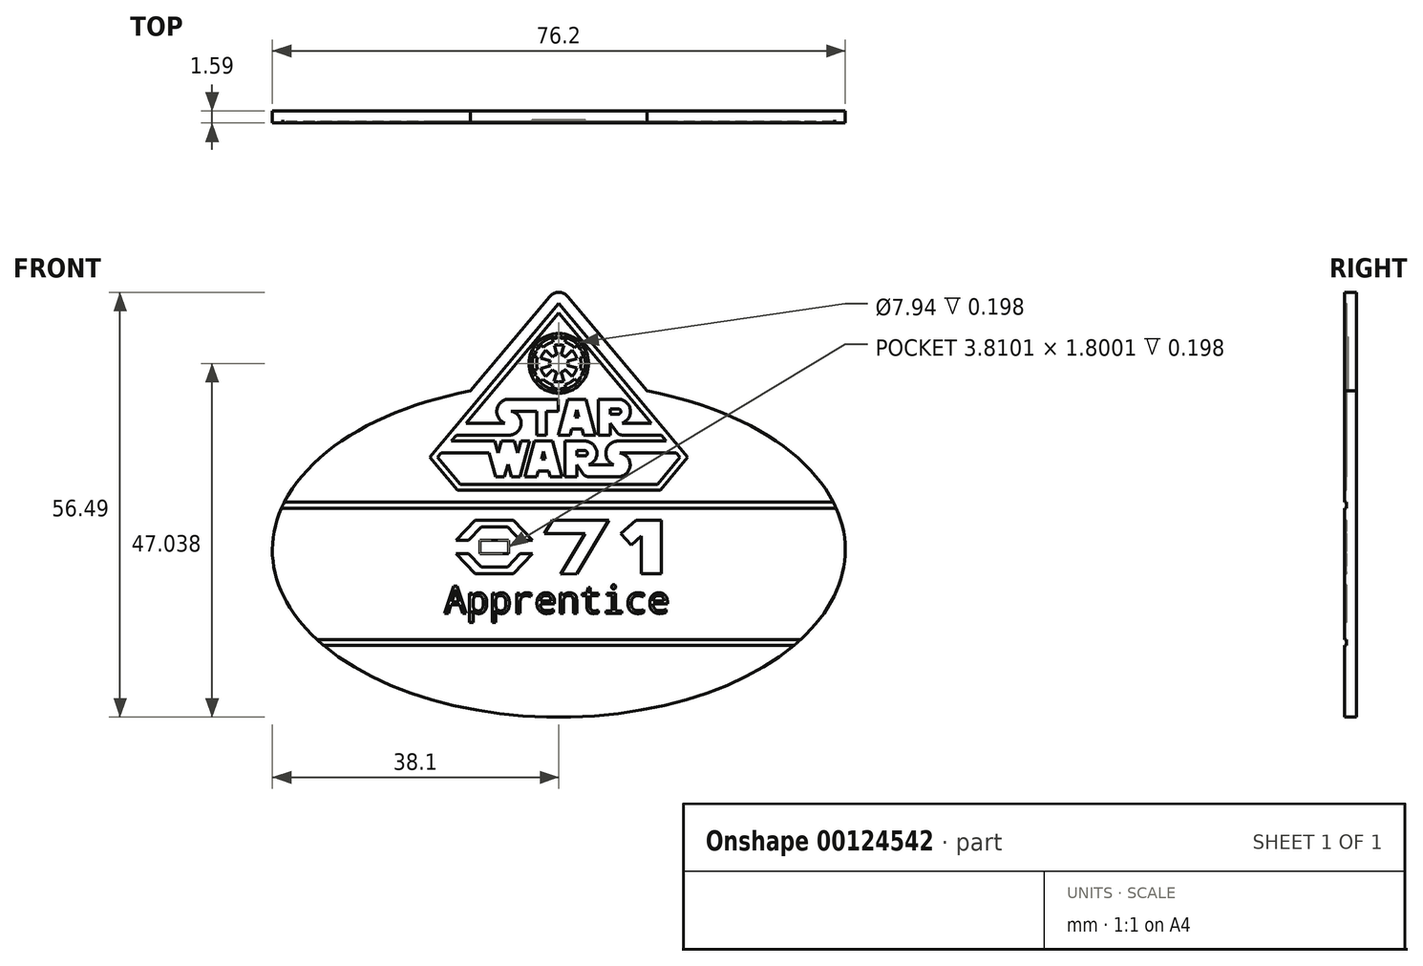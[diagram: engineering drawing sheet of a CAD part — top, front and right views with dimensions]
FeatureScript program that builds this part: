
annotation { "Feature Type Name" : "Feature", "Feature Type Description" : "" }
export const myFeature = defineFeature(function(context is Context, id is Id, definition is map)
    precondition{}
    {
        {
            var Q0;
            Q0=qCreatedBy(makeId("Front.planeOp"),FACE);
            var sketch = newSketch(context, id + "F0", { "sketchPlane" : qUnion([Q0])});
            skLineSegment(sketch, "E0", {"start": v(36.9, 5.56) * mm, "end": v(-36.9, 5.56) * mm});
            skLineSegment(sketch, "E1", {"start": v(-36.51, 6.35) * mm, "end": v(36.51, 6.35) * mm});
            skPoint(sketch, "E2", {"position": v(0, 35.14) * mm});
            skLineSegment(sketch, "E3.trimOffspring", {"start": v(0, 22.22) * mm, "end": v(0, 22.22) * mm});
            skPoint(sketch, "E4", {"position": v(0, -22.23) * mm});
            skPoint(sketch, "E5", {"position": v(-13.5, 7.94) * mm});
            skPoint(sketch, "E6", {"position": v(13.5, 7.94) * mm});
            skLineSegment(sketch, "E7", {"start": v(0, 35.14) * mm, "end": v(11.75, 21.14) * mm});
            skLineSegment(sketch, "E8", {"start": v(0, 35.14) * mm, "end": v(-11.75, 21.14) * mm});
            skEllipticalArc(sketch, "E9", {});
            skLineSegment(sketch, "E10", {"start": v(0, 32.76) * mm, "end": v(-17.16, 12.3) * mm});
            skLineSegment(sketch, "E11", {"start": v(0, 32.76) * mm, "end": v(17.16, 12.3) * mm});
            skPoint(sketch, "E12", {"position": v(0, 7.97) * mm});
            skLineSegment(sketch, "E13", {"start": v(-13.5, 7.94) * mm, "end": v(-17.16, 12.3) * mm});
            skLineSegment(sketch, "E14", {"start": v(13.5, 7.94) * mm, "end": v(17.16, 12.3) * mm});
            skLineSegment(sketch, "E15", {"start": v(-13.5, 7.94) * mm, "end": v(13.5, 7.94) * mm});
            skLineSegment(sketch, "E16.trimOffspring", {"start": v(0, 7.97) * mm, "end": v(0, 7.94) * mm});
            skLineSegment(sketch, "E17.trimOffspring", {"start": v(0, 0) * mm, "end": v(0, 0) * mm});
            skLineSegment(sketch, "E18.trimOffspring", {"start": v(0, -22.23) * mm, "end": v(0, -22.23) * mm});
            skLineSegment(sketch, "E19.0", {"start": v(-13.12, 8.73) * mm, "end": v(-16.13, 12.3) * mm});
            skLineSegment(sketch, "E19.1", {"start": v(0, 31.53) * mm, "end": v(-16.13, 12.3) * mm});
            skLineSegment(sketch, "E19.2", {"start": v(-13.12, 8.73) * mm, "end": v(13.12, 8.73) * mm});
            skLineSegment(sketch, "E19.3", {"start": v(13.12, 8.73) * mm, "end": v(16.13, 12.3) * mm});
            skLineSegment(sketch, "E19.4", {"start": v(0, 31.53) * mm, "end": v(16.13, 12.3) * mm});
            skCircle(sketch, "E20", {"center": v(0, 24.8) * mm, "radius": 3.97 * mm});
            skLineSegment(sketch, "E21", {"start": v(0, 18.51) * mm, "end": v(0, 7.97) * mm});
            skLineSegment(sketch, "E22", {"start": v(-31.27, -12.7) * mm, "end": v(31.27, -12.7) * mm});
            skLineSegment(sketch, "E23", {"start": v(-32.17, -11.9) * mm, "end": v(32.17, -11.9) * mm});
            skArc(sketch, "E24", {"start": v(2.98, 26.72) * mm, "mid": v(1.77, 27.87) * mm, "end": v(0.17, 28.34) * mm});
            skArc(sketch, "E25", {"start": v(-0.17, 28.19) * mm, "mid": v(-0.52, 28.15) * mm, "end": v(-0.86, 28.08) * mm});
            skArc(sketch, "E26", {"start": v(-1.73, 26.57) * mm, "mid": v(-2.13, 26.06) * mm, "end": v(-2.38, 25.46) * mm});
            skArc(sketch, "E27", {"start": v(-0.74, 27.67) * mm, "mid": v(-1.45, 27.38) * mm, "end": v(-2.06, 26.92) * mm});
            skLineSegment(sketch, "E28", {"start": v(-0.17, 28.34) * mm, "end": v(-0.17, 28.19) * mm});
            skLineSegment(sketch, "E29", {"start": v(0.17, 28.34) * mm, "end": v(0.17, 28.19) * mm});
            skLineSegment(sketch, "E30", {"start": v(2.98, 26.72) * mm, "end": v(2.85, 26.64) * mm});
            skLineSegment(sketch, "E31", {"start": v(3.15, 26.42) * mm, "end": v(3.01, 26.35) * mm});
            skLineSegment(sketch, "E32", {"start": v(3.02, 23.28) * mm, "end": v(3.16, 23.21) * mm});
            skLineSegment(sketch, "E33", {"start": v(2.86, 23) * mm, "end": v(2.99, 22.91) * mm});
            skLineSegment(sketch, "E34", {"start": v(-0.86, 28.08) * mm, "end": v(-0.74, 27.67) * mm});
            skLineSegment(sketch, "E35", {"start": v(0.91, 28.07) * mm, "end": v(0.8, 27.65) * mm});
            skLineSegment(sketch, "E36.trimOffspring", {"start": v(0.67, 27.19) * mm, "end": v(0.33, 25.96) * mm});
            skLineSegment(sketch, "E37.trimOffspring", {"start": v(-0.61, 27.2) * mm, "end": v(-0.28, 25.98) * mm});
            skLineSegment(sketch, "E38", {"start": v(-0.87, 21.54) * mm, "end": v(-0.76, 21.95) * mm});
            skLineSegment(sketch, "E39", {"start": v(0.32, 23.65) * mm, "end": v(0.66, 22.43) * mm});
            skLineSegment(sketch, "E40", {"start": v(0.87, 23.98) * mm, "end": v(1.76, 23.07) * mm});
            skLineSegment(sketch, "E41", {"start": v(1.16, 24.5) * mm, "end": v(2.39, 24.18) * mm});
            skLineSegment(sketch, "E42", {"start": v(1.16, 25.13) * mm, "end": v(2.39, 25.45) * mm});
            skLineSegment(sketch, "E43", {"start": v(2.4, 27.19) * mm, "end": v(2.1, 26.89) * mm});
            skLineSegment(sketch, "E44", {"start": v(-2.36, 27.24) * mm, "end": v(-2.06, 26.92) * mm});
            skLineSegment(sketch, "E45", {"start": v(-3.27, 25.7) * mm, "end": v(-2.85, 25.59) * mm});
            skLineSegment(sketch, "E46", {"start": v(-3.27, 23.94) * mm, "end": v(-2.85, 24.05) * mm});
            skLineSegment(sketch, "E47", {"start": v(-2.4, 22.41) * mm, "end": v(-2.09, 22.72) * mm});
            skLineSegment(sketch, "E48.trimOffspring", {"start": v(-0.17, 21.43) * mm, "end": v(-0.17, 21.28) * mm});
            skArc(sketch, "E49.trimOffspring", {"start": v(2.85, 26.64) * mm, "mid": v(2.64, 26.93) * mm, "end": v(2.4, 27.19) * mm});
            skArc(sketch, "E50.trimOffspring", {"start": v(2.1, 26.89) * mm, "mid": v(1.5, 27.35) * mm, "end": v(0.8, 27.65) * mm});
            skLineSegment(sketch, "E51.trimOffspring", {"start": v(1.76, 26.55) * mm, "end": v(0.85, 25.65) * mm});
            skLineSegment(sketch, "E52.trimOffspring", {"start": v(2.85, 25.57) * mm, "end": v(3.27, 25.68) * mm});
            skLineSegment(sketch, "E53.trimOffspring", {"start": v(0.32, 23.65) * mm, "end": v(0.32, 23.65) * mm});
            skArc(sketch, "E54.trimOffspring", {"start": v(0.8, 21.96) * mm, "mid": v(1.5, 22.26) * mm, "end": v(2.1, 22.73) * mm});
            skArc(sketch, "E55.trimOffspring", {"start": v(0.17, 21.43) * mm, "mid": v(0.55, 21.47) * mm, "end": v(0.91, 21.55) * mm});
            skArc(sketch, "E56.trimOffspring", {"start": v(0.17, 21.28) * mm, "mid": v(1.78, 21.75) * mm, "end": v(2.99, 22.91) * mm});
            skArc(sketch, "E57.trimOffspring", {"start": v(-0.17, 28.34) * mm, "mid": v(-1.76, 27.87) * mm, "end": v(-2.97, 26.74) * mm});
            skLineSegment(sketch, "E58.trimOffspring", {"start": v(0.8, 21.96) * mm, "end": v(0.91, 21.55) * mm});
            skLineSegment(sketch, "E59.trimOffspring", {"start": v(-0.63, 22.42) * mm, "end": v(-0.3, 23.64) * mm});
            skLineSegment(sketch, "E60.trimOffspring", {"start": v(2.1, 22.73) * mm, "end": v(2.4, 22.42) * mm});
            skArc(sketch, "E61.trimOffspring", {"start": v(2.86, 24.06) * mm, "mid": v(2.95, 24.82) * mm, "end": v(2.85, 25.57) * mm});
            skArc(sketch, "E62.trimOffspring", {"start": v(3.02, 23.28) * mm, "mid": v(3.17, 23.61) * mm, "end": v(3.27, 23.95) * mm});
            skArc(sketch, "E63.trimOffspring", {"start": v(3.16, 23.21) * mm, "mid": v(3.54, 24.82) * mm, "end": v(3.15, 26.42) * mm});
            skArc(sketch, "E64.trimOffspring", {"start": v(0.67, 27.19) * mm, "mid": v(0.03, 27.28) * mm, "end": v(-0.61, 27.2) * mm});
            skArc(sketch, "E65.trimOffspring", {"start": v(2.39, 25.45) * mm, "mid": v(2.14, 26.04) * mm, "end": v(1.76, 26.55) * mm});
            skLineSegment(sketch, "E66.trimOffspring", {"start": v(-1.73, 26.57) * mm, "end": v(-0.85, 25.66) * mm});
            skArc(sketch, "E67.trimOffspring", {"start": v(-2.85, 25.59) * mm, "mid": v(-2.95, 24.82) * mm, "end": v(-2.85, 24.05) * mm});
            skLineSegment(sketch, "E68.trimOffspring", {"start": v(-2.38, 25.46) * mm, "end": v(-1.15, 25.14) * mm});
            skLineSegment(sketch, "E69.trimOffspring", {"start": v(-2.39, 24.17) * mm, "end": v(-1.16, 24.48) * mm});
            skArc(sketch, "E70.trimOffspring", {"start": v(-2.09, 22.72) * mm, "mid": v(-1.47, 22.25) * mm, "end": v(-0.76, 21.95) * mm});
            skLineSegment(sketch, "E71.trimOffspring", {"start": v(-1.75, 23.06) * mm, "end": v(-0.85, 23.96) * mm});
            skLineSegment(sketch, "E72.trimOffspring", {"start": v(2.86, 24.06) * mm, "end": v(3.27, 23.95) * mm});
            skLineSegment(sketch, "E73", {"start": v(-2.97, 26.74) * mm, "end": v(-2.83, 26.67) * mm});
            skLineSegment(sketch, "E74", {"start": v(-3.15, 26.42) * mm, "end": v(-3, 26.37) * mm});
            skArc(sketch, "E75.trimOffspring", {"start": v(-3.15, 26.42) * mm, "mid": v(-3.54, 24.8) * mm, "end": v(-3.14, 23.19) * mm});
            skArc(sketch, "E76.trimOffspring", {"start": v(-3, 26.37) * mm, "mid": v(-3.15, 26.04) * mm, "end": v(-3.27, 25.7) * mm});
            skLineSegment(sketch, "E77", {"start": v(0.17, 21.43) * mm, "end": v(0.17, 21.28) * mm});
            skLineSegment(sketch, "E78", {"start": v(-3.14, 23.19) * mm, "end": v(-3.01, 23.26) * mm});
            skLineSegment(sketch, "E79", {"start": v(-2.97, 22.89) * mm, "end": v(-2.84, 22.96) * mm});
            skArc(sketch, "E80.trimOffspring", {"start": v(-2.84, 22.96) * mm, "mid": v(-2.63, 22.68) * mm, "end": v(-2.4, 22.41) * mm});
            skArc(sketch, "E81.trimOffspring", {"start": v(-2.97, 22.89) * mm, "mid": v(-1.77, 21.74) * mm, "end": v(-0.17, 21.28) * mm});
            skArc(sketch, "E82.trimOffspring", {"start": v(-3.27, 23.94) * mm, "mid": v(-3.16, 23.6) * mm, "end": v(-3.01, 23.26) * mm});
            skArc(sketch, "E83.trimOffspring", {"start": v(-2.39, 24.17) * mm, "mid": v(-2.14, 23.57) * mm, "end": v(-1.75, 23.06) * mm});
            skLineSegment(sketch, "E84.trimOffspring", {"start": v(1.16, 24.5) * mm, "end": v(1.16, 24.5) * mm});
            skArc(sketch, "E85", {"start": v(-0.28, 25.98) * mm, "mid": v(-0.58, 25.86) * mm, "end": v(-0.85, 25.66) * mm});
            skArc(sketch, "E86.trimOffspring", {"start": v(-1.15, 25.14) * mm, "mid": v(-1.2, 24.81) * mm, "end": v(-1.16, 24.48) * mm});
            skArc(sketch, "E87.trimOffspring", {"start": v(0.85, 25.65) * mm, "mid": v(0.61, 25.84) * mm, "end": v(0.33, 25.96) * mm});
            skArc(sketch, "E88.trimOffspring", {"start": v(1.16, 24.5) * mm, "mid": v(1.2, 24.82) * mm, "end": v(1.16, 25.13) * mm});
            skArc(sketch, "E89.trimOffspring", {"start": v(0.32, 23.65) * mm, "mid": v(0.62, 23.78) * mm, "end": v(0.87, 23.98) * mm});
            skArc(sketch, "E90.trimOffspring", {"start": v(-0.85, 23.96) * mm, "mid": v(-0.6, 23.76) * mm, "end": v(-0.3, 23.64) * mm});
            skArc(sketch, "E91.trimOffspring", {"start": v(-0.63, 22.42) * mm, "mid": v(0.02, 22.34) * mm, "end": v(0.66, 22.43) * mm});
            skArc(sketch, "E92.trimOffspring", {"start": v(1.76, 23.07) * mm, "mid": v(2.15, 23.59) * mm, "end": v(2.39, 24.18) * mm});
            skArc(sketch, "E93.trimOffspring", {"start": v(-2.36, 27.24) * mm, "mid": v(-2.6, 26.96) * mm, "end": v(-2.83, 26.67) * mm});
            skArc(sketch, "E94.trimOffspring", {"start": v(0.91, 28.07) * mm, "mid": v(0.55, 28.15) * mm, "end": v(0.17, 28.19) * mm});
            skArc(sketch, "E95.trimOffspring", {"start": v(3.27, 25.68) * mm, "mid": v(3.16, 26.02) * mm, "end": v(3.01, 26.35) * mm});
            skArc(sketch, "E96.trimOffspring", {"start": v(2.4, 22.42) * mm, "mid": v(2.64, 22.7) * mm, "end": v(2.86, 23) * mm});
            skArc(sketch, "E97.trimOffspring", {"start": v(-0.87, 21.54) * mm, "mid": v(-0.53, 21.46) * mm, "end": v(-0.17, 21.43) * mm});
            const initialGuessF0  = {"E9": [0, 0, 1, 0, 0.0381, 0.022225, 1.8842338584766234, 1.25735879511317]};
            skSetInitialGuess(sketch, initialGuessF0);
            skSolve(sketch);
        }
        {
            var Q0;
            {var subQ0=sQuery(id+"F0.wireOp",EDGE,"E22");Q0=makeQuery(id+"F0.imprint","IMPRINT",FACE,{"disambiguationData":[TD([[makeQuery(id+"F0.imprint","IMPRINT",EDGE,{"derivedFrom":subQ0}),-1.0]])]});}
            var Q1;
            {var subQ4=sQuery(id+"F0.wireOp",EDGE,"E23");Q1=makeQuery(id+"F0.imprint","IMPRINT",FACE,{"disambiguationData":[TD([[makeQuery(id+"F0.imprint","IMPRINT",EDGE,{"derivedFrom":subQ4}),1.0]])]});}
            var Q2;
            {var subQ8=sQuery(id+"F0.wireOp",EDGE,"E7");Q2=makeQuery(id+"F0.imprint","IMPRINT",FACE,{"disambiguationData":[TD([[makeQuery(id+"F0.imprint","IMPRINT",EDGE,{"derivedFrom":subQ8}),-1.0]])]});}
            var Q3;
            {var subQ10=sQuery(id+"F0.wireOp",EDGE,"E19.0");Q3=makeQuery(id+"F0.imprint","IMPRINT",FACE,{"disambiguationData":[TD([[makeQuery(id+"F0.imprint","IMPRINT",EDGE,{"derivedFrom":subQ10}),-1.0]])]});}
            extrude(context, id + "F1", {"entities" : qUnion([Q0, Q1, Q2, Q3]), "depth" : 1.59 * mm});
        }
        {
            var Q0;
            {var subQ0=sQuery(id+"F0.wireOp",EDGE,"E22");Q0=makeQuery(id+"F0.imprint","IMPRINT",FACE,{"disambiguationData":[TD([[makeQuery(id+"F0.imprint","IMPRINT",EDGE,{"derivedFrom":subQ0}),1.0]])]});}
            var Q1;
            {var subQ0=sQuery(id+"F0.wireOp",EDGE,"E9");var subQ1=sQuery(id+"F0.wireOp",EDGE,"E0");var subQ2=makeQuery(id+"F0.imprint","INTERSECT",VERTEX,{"disambiguationData":[OD(0.0)],"derivedFrom":[subQ1,subQ0]});Q1=makeQuery(id+"F0.imprint","IMPRINT",FACE,{"disambiguationData":[TD([[makeQuery(id+"F0.imprint","IMPRINT",EDGE,{"disambiguationData":[TD([[subQ2,-1.0]])],"derivedFrom":subQ1}),-1.0]])]});}
            var Q2;
            Q2=makeQuery(id+"F0.imprint","IMPRINT",FACE,{"disambiguationData":[TD([[makeQuery(id+"F0.imprint","IMPRINT",EDGE,{"derivedFrom":sQuery(id+"F0.wireOp",EDGE,"E10")}),1.0]])]});
            extrude(context, id + "F2", {"entities" : qUnion([Q0, Q1, Q2]), "operationType" : NewBodyOperationType.ADD, "depth" : 1.39 * mm});
        }
        {
            var Q0;
            Q0=makeQuery(id+"F0.imprint","IMPRINT",FACE,{"disambiguationData":[TD([[makeQuery(id+"F0.imprint","IMPRINT",EDGE,{"derivedFrom":sQuery(id+"F0.wireOp",EDGE,"E20")}),1.0]])]});
            extrude(context, id + "F3", {"entities" : qUnion([Q0]), "operationType" : NewBodyOperationType.ADD, "depth" : 1.39 * mm});
        }
        {
            var Q0;
            Q0=makeQuery(id+"F0.imprint","IMPRINT",FACE,{"disambiguationData":[TD([[makeQuery(id+"F0.imprint","IMPRINT",EDGE,{"derivedFrom":sQuery(id+"F0.wireOp",EDGE,"E26")}),1.0]])]});
            var Q1;
            Q1=makeQuery(id+"F0.imprint","IMPRINT",FACE,{"disambiguationData":[TD([[makeQuery(id+"F0.imprint","IMPRINT",EDGE,{"derivedFrom":sQuery(id+"F0.wireOp",EDGE,"E25")}),-1.0]])]});
            var Q2;
            Q2=makeQuery(id+"F0.imprint","IMPRINT",FACE,{"disambiguationData":[TD([[makeQuery(id+"F0.imprint","IMPRINT",EDGE,{"derivedFrom":sQuery(id+"F0.wireOp",EDGE,"E45")}),-1.0]])]});
            var Q3;
            Q3=makeQuery(id+"F0.imprint","IMPRINT",FACE,{"disambiguationData":[TD([[makeQuery(id+"F0.imprint","IMPRINT",EDGE,{"derivedFrom":sQuery(id+"F0.wireOp",EDGE,"E24")}),1.0]])]});
            var Q4;
            Q4=makeQuery(id+"F0.imprint","IMPRINT",FACE,{"disambiguationData":[TD([[makeQuery(id+"F0.imprint","IMPRINT",EDGE,{"derivedFrom":sQuery(id+"F0.wireOp",EDGE,"E31")}),1.0]])]});
            var Q5;
            Q5=makeQuery(id+"F0.imprint","IMPRINT",FACE,{"disambiguationData":[TD([[makeQuery(id+"F0.imprint","IMPRINT",EDGE,{"derivedFrom":sQuery(id+"F0.wireOp",EDGE,"E33")}),-1.0]])]});
            var Q6;
            Q6=makeQuery(id+"F0.imprint","IMPRINT",FACE,{"disambiguationData":[TD([[makeQuery(id+"F0.imprint","IMPRINT",EDGE,{"derivedFrom":sQuery(id+"F0.wireOp",EDGE,"E38")}),1.0]])]});
            extrude(context, id + "F4", {"entities" : qUnion([Q0, Q1, Q2, Q3, Q4, Q5, Q6]), "operationType" : NewBodyOperationType.ADD, "depth" : 1.2 * mm});
        }
        {
            var Q0;
            Q0=makeQuery(id+"F1.opExtrude","CAP_FACE",FACE,{"disambiguationData":[OSD([sQuery(id+"F0.wireOp",EDGE,"E19.0"),sQuery(id+"F0.wireOp",EDGE,"E19.1"),sQuery(id+"F0.wireOp",EDGE,"E19.2"),sQuery(id+"F0.wireOp",EDGE,"E19.3"),sQuery(id+"F0.wireOp",EDGE,"E19.4"),sQuery(id+"F0.wireOp",EDGE,"E20")])],"isStart":false});
            var sketch = newSketch(context, id + "F5", { "sketchPlane" : qUnion([Q0])});
            skLineSegment(sketch, "E98", {"start": v(-8.42, 9.73) * mm, "end": v(-7.23, 9.73) * mm});
            skLineSegment(sketch, "E99", {"start": v(-2.95, 15.28) * mm, "end": v(-1.68, 15.28) * mm});
            skLineSegment(sketch, "E100", {"start": v(-0.1, 15.28) * mm, "end": v(1.5, 15.28) * mm});
            skLineSegment(sketch, "E101", {"start": v(-0.1, 15.28) * mm, "end": v(1.18, 20.03) * mm});
            skLineSegment(sketch, "E102", {"start": v(4.88, 15.28) * mm, "end": v(3.6, 20.03) * mm});
            skLineSegment(sketch, "E103", {"start": v(3.6, 20.03) * mm, "end": v(1.18, 20.03) * mm});
            skLineSegment(sketch, "E104", {"start": v(5.28, 15.28) * mm, "end": v(5.28, 20.05) * mm});
            skLineSegment(sketch, "E105", {"start": v(6.86, 16.87) * mm, "end": v(7.7, 15.66) * mm});
            skLineSegment(sketch, "E106", {"start": v(6.86, 16.87) * mm, "end": v(6.86, 15.28) * mm});
            skLineSegment(sketch, "E107", {"start": v(5.28, 15.28) * mm, "end": v(6.86, 15.28) * mm});
            skArc(sketch, "E108", {"start": v(8.45, 16.87) * mm, "mid": v(9.5, 18.7) * mm, "end": v(7.88, 20.05) * mm});
            skArc(sketch, "E109.0", {"start": v(8.01, 18.06) * mm, "mid": v(8.25, 18.48) * mm, "end": v(7.88, 18.78) * mm});
            skLineSegment(sketch, "E110", {"start": v(7.88, 18.78) * mm, "end": v(6.86, 18.78) * mm});
            skLineSegment(sketch, "E111", {"start": v(6.86, 18.06) * mm, "end": v(8.01, 18.06) * mm});
            skLineSegment(sketch, "E112", {"start": v(6.86, 18.78) * mm, "end": v(6.86, 18.06) * mm});
            skLineSegment(sketch, "E113", {"start": v(12.3, 16.87) * mm, "end": v(13.63, 15.28) * mm});
            skLineSegment(sketch, "E114", {"start": v(13.63, 15.28) * mm, "end": v(8.42, 15.28) * mm});
            skLineSegment(sketch, "E115", {"start": v(8.45, 16.87) * mm, "end": v(12.3, 16.87) * mm});
            skArc(sketch, "E116", {"start": v(7.7, 15.66) * mm, "mid": v(8.02, 15.4) * mm, "end": v(8.42, 15.28) * mm});
            skLineSegment(sketch, "E117", {"start": v(-1.68, 15.28) * mm, "end": v(-1.68, 18.46) * mm});
            skLineSegment(sketch, "E118", {"start": v(-2.95, 15.28) * mm, "end": v(-2.95, 18.46) * mm});
            skLineSegment(sketch, "E119", {"start": v(-1.68, 18.46) * mm, "end": v(-0.1, 18.46) * mm});
            skLineSegment(sketch, "E120", {"start": v(-0.1, 18.46) * mm, "end": v(-0.1, 20.05) * mm});
            skLineSegment(sketch, "E121", {"start": v(-13.63, 15.28) * mm, "end": v(-6.6, 15.28) * mm});
            skLineSegment(sketch, "E122", {"start": v(-2.95, 18.46) * mm, "end": v(-6.34, 18.46) * mm});
            skLineSegment(sketch, "E123.trimOffspring", {"start": v(3.3, 15.28) * mm, "end": v(4.88, 15.28) * mm});
            skLineSegment(sketch, "E124.trimOffspring", {"start": v(5.28, 20.05) * mm, "end": v(7.88, 20.05) * mm});
            skLineSegment(sketch, "E125", {"start": v(-4.54, 9.73) * mm, "end": v(-3.26, 14.49) * mm});
            skLineSegment(sketch, "E126", {"start": v(0.43, 9.73) * mm, "end": v(-0.84, 14.49) * mm});
            skLineSegment(sketch, "E127", {"start": v(1.7, 16.08) * mm, "end": v(3.08, 16.08) * mm});
            skLineSegment(sketch, "E128", {"start": v(1.5, 15.28) * mm, "end": v(1.7, 16.08) * mm});
            skLineSegment(sketch, "E129", {"start": v(3.3, 15.28) * mm, "end": v(3.08, 16.08) * mm});
            skLineSegment(sketch, "E130", {"start": v(2.13, 17.66) * mm, "end": v(2.65, 17.66) * mm});
            skLineSegment(sketch, "E131.trimOffspring", {"start": v(2.13, 17.66) * mm, "end": v(2.4, 18.63) * mm});
            skLineSegment(sketch, "E132.trimOffspring", {"start": v(2.65, 17.66) * mm, "end": v(2.4, 18.63) * mm});
            skLineSegment(sketch, "E133", {"start": v(-2.95, 9.73) * mm, "end": v(-2.74, 10.52) * mm});
            skLineSegment(sketch, "E134", {"start": v(-1.15, 9.73) * mm, "end": v(-1.37, 10.52) * mm});
            skLineSegment(sketch, "E135", {"start": v(-2.74, 10.52) * mm, "end": v(-1.37, 10.52) * mm});
            skLineSegment(sketch, "E136.trimOffspring", {"start": v(-2.31, 12.1) * mm, "end": v(-1.8, 12.1) * mm});
            skLineSegment(sketch, "E137", {"start": v(-4.54, 9.73) * mm, "end": v(-2.95, 9.73) * mm});
            skLineSegment(sketch, "E138", {"start": v(-1.15, 9.73) * mm, "end": v(0.43, 9.73) * mm});
            skLineSegment(sketch, "E139.trimOffspring", {"start": v(-2.31, 12.1) * mm, "end": v(-2.05, 13.08) * mm});
            skLineSegment(sketch, "E140.trimOffspring", {"start": v(-1.8, 12.1) * mm, "end": v(-2.05, 13.08) * mm});
            skLineSegment(sketch, "E141.trimOffspring", {"start": v(-3.26, 14.49) * mm, "end": v(-0.84, 14.49) * mm});
            skLineSegment(sketch, "E142.trimOffspring", {"start": v(0.83, 14.49) * mm, "end": v(3.44, 14.49) * mm});
            skLineSegment(sketch, "E143", {"start": v(0.83, 9.73) * mm, "end": v(0.83, 14.49) * mm});
            skLineSegment(sketch, "E144", {"start": v(2.42, 9.73) * mm, "end": v(2.42, 11.31) * mm});
            skLineSegment(sketch, "E145", {"start": v(4, 11.31) * mm, "end": v(7.32, 11.31) * mm});
            skLineSegment(sketch, "E146", {"start": v(2.42, 11.31) * mm, "end": v(3.26, 10.12) * mm});
            skArc(sketch, "E147", {"start": v(4, 11.31) * mm, "mid": v(5.04, 13.14) * mm, "end": v(3.44, 14.49) * mm});
            skLineSegment(sketch, "E148", {"start": v(2.42, 13.22) * mm, "end": v(3.43, 13.22) * mm});
            skLineSegment(sketch, "E149", {"start": v(2.42, 12.5) * mm, "end": v(3.56, 12.5) * mm});
            skArc(sketch, "E150", {"start": v(3.56, 12.5) * mm, "mid": v(3.8, 12.92) * mm, "end": v(3.43, 13.22) * mm});
            skLineSegment(sketch, "E151.trimOffspring", {"start": v(2.42, 12.5) * mm, "end": v(2.42, 13.22) * mm});
            skLineSegment(sketch, "E152.trimOffspring", {"start": v(0.83, 9.73) * mm, "end": v(2.42, 9.73) * mm});
            skPoint(sketch, "E153.visualSharp", {"position": v(3.53, 9.73) * mm});
            skArc(sketch, "E153.filletArc", {"start": v(3.26, 10.12) * mm, "mid": v(3.58, 9.83) * mm, "end": v(4, 9.73) * mm});
            skArc(sketch, "E154.MirrorCS", {"start": v(7.32, 11.31) * mm, "mid": v(6.28, 13.14) * mm, "end": v(7.88, 14.49) * mm});
            skLineSegment(sketch, "E155", {"start": v(15.63, 12.9) * mm, "end": v(8.15, 12.9) * mm});
            skArc(sketch, "E156.MirrorCS", {"start": v(7.9, 9.73) * mm, "mid": v(9.47, 11.1) * mm, "end": v(8.33, 12.85) * mm});
            skLineSegment(sketch, "E157", {"start": v(8.33, 12.85) * mm, "end": v(8.15, 12.9) * mm});
            skLineSegment(sketch, "E158", {"start": v(7.9, 9.73) * mm, "end": v(4, 9.73) * mm});
            skLineSegment(sketch, "E159", {"start": v(-6.34, 18.46) * mm, "end": v(-6.16, 18.41) * mm});
            skArc(sketch, "E160", {"start": v(-6.16, 18.41) * mm, "mid": v(-5.01, 16.66) * mm, "end": v(-6.6, 15.28) * mm});
            skPoint(sketch, "E161", {"position": v(-7.17, 16.87) * mm});
            skLineSegment(sketch, "E162", {"start": v(-0.1, 20.05) * mm, "end": v(-6.6, 20.05) * mm});
            skLineSegment(sketch, "E163", {"start": v(-7.17, 16.87) * mm, "end": v(-12.3, 16.87) * mm});
            skLineSegment(sketch, "E164", {"start": v(-12.3, 16.87) * mm, "end": v(-13.63, 15.28) * mm});
            skArc(sketch, "E165", {"start": v(-6.6, 20.05) * mm, "mid": v(-8.22, 18.7) * mm, "end": v(-7.17, 16.87) * mm});
            skLineSegment(sketch, "E166.trimOffspring", {"start": v(7.88, 14.49) * mm, "end": v(14.3, 14.49) * mm});
            skLineSegment(sketch, "E167", {"start": v(-3.85, 14.49) * mm, "end": v(-5.13, 9.73) * mm});
            skLineSegment(sketch, "E168", {"start": v(-3.85, 14.49) * mm, "end": v(-5.05, 14.49) * mm});
            skLineSegment(sketch, "E169", {"start": v(-15.63, 12.9) * mm, "end": v(-9.27, 12.9) * mm});
            skLineSegment(sketch, "E170", {"start": v(-5.47, 12.9) * mm, "end": v(-5.9, 14.49) * mm});
            skLineSegment(sketch, "E171", {"start": v(-6.32, 9.73) * mm, "end": v(-6.77, 11.41) * mm});
            skLineSegment(sketch, "E172", {"start": v(-6.77, 11.41) * mm, "end": v(-7.23, 9.73) * mm});
            skLineSegment(sketch, "E173", {"start": v(-9.27, 12.9) * mm, "end": v(-8.42, 9.73) * mm});
            skLineSegment(sketch, "E174", {"start": v(-8.08, 12.9) * mm, "end": v(-7.65, 14.49) * mm});
            skLineSegment(sketch, "E175.trimOffspring", {"start": v(-8.08, 12.9) * mm, "end": v(-8.5, 14.49) * mm});
            skLineSegment(sketch, "E176", {"start": v(-5.47, 12.9) * mm, "end": v(-5.05, 14.49) * mm});
            skLineSegment(sketch, "E177.trimOffspring", {"start": v(-8.5, 14.49) * mm, "end": v(-14.3, 14.49) * mm});
            skLineSegment(sketch, "E178.trimOffspring", {"start": v(-5.9, 14.49) * mm, "end": v(-7.65, 14.49) * mm});
            skLineSegment(sketch, "E179.trimOffspring", {"start": v(-6.32, 9.73) * mm, "end": v(-5.13, 9.73) * mm});
            skLineSegment(sketch, "E180", {"start": v(-14.3, 14.49) * mm, "end": v(-15.63, 12.9) * mm});
            skSolve(sketch);
        }
        {
            var Q0;
            Q0=makeQuery(id+"F1.opExtrude","SWEPT_EDGE",EDGE,{"disambiguationData":[OSD([sQuery(id+"F0.wireOp",EDGE,"E7"),sQuery(id+"F0.wireOp",EDGE,"E8")])]});
            fillet(context, id + "F6", {"entities" : qUnion([Q0]), "radius" : 1.59 * mm, "tangentPropagation" : true, "allowEdgeOverflow" : false});
        }
        {
            var Q0;
            Q0=makeQuery(id+"F5.imprint","IMPRINT",FACE,{"disambiguationData":[TD([[makeQuery(id+"F5.imprint","IMPRINT",EDGE,{"derivedFrom":sQuery(id+"F5.wireOp",EDGE,"E99")}),1.0]])]});
            var Q1;
            Q1=makeQuery(id+"F5.imprint","IMPRINT",FACE,{"disambiguationData":[TD([[makeQuery(id+"F5.imprint","IMPRINT",EDGE,{"derivedFrom":sQuery(id+"F5.wireOp",EDGE,"E100")}),1.0]])]});
            var Q2;
            {var subQ1=sQuery(id+"F5.wireOp",EDGE,"E104");Q2=makeQuery(id+"F5.imprint","IMPRINT",FACE,{"disambiguationData":[TD([[makeQuery(id+"F5.imprint","IMPRINT",EDGE,{"derivedFrom":subQ1}),-1.0]])]});}
            var Q3;
            Q3=makeQuery(id+"F5.imprint","IMPRINT",FACE,{"disambiguationData":[TD([[makeQuery(id+"F5.imprint","IMPRINT",EDGE,{"derivedFrom":sQuery(id+"F5.wireOp",EDGE,"E125")}),-1.0]])]});
            var Q4;
            {var subQ0=sQuery(id+"F5.wireOp",EDGE,"E143");Q4=makeQuery(id+"F5.imprint","IMPRINT",FACE,{"disambiguationData":[TD([[makeQuery(id+"F5.imprint","IMPRINT",EDGE,{"derivedFrom":subQ0}),-1.0]])]});}
            var Q5;
            Q5=makeQuery(id+"F5.imprint","IMPRINT",FACE,{"disambiguationData":[TD([[makeQuery(id+"F5.imprint","IMPRINT",EDGE,{"derivedFrom":sQuery(id+"F5.wireOp",EDGE,"E98")}),1.0]])]});
            extrude(context, id + "F7", {"entities" : qUnion([Q0, Q1, Q2, Q3, Q4, Q5]), "operationType" : NewBodyOperationType.REMOVE, "oppositeDirection" : true, "depth" : 0.2 * mm});
        }
        {
            var Q0;
            Q0=makeQuery(id+"F1.opExtrude","CAP_FACE",FACE,{"disambiguationData":[OSD([sQuery(id+"F0.wireOp",EDGE,"E0"),sQuery(id+"F0.wireOp",EDGE,"E9"),sQuery(id+"F0.wireOp",EDGE,"E23")])],"isStart":false});
            var sketch = newSketch(context, id + "F8", { "sketchPlane" : qUnion([Q0])});
            skText(sketch, "E181", { "text": "Apprentice", "fontName": "DroidSansMono.ttf"});
            skLineSegment(sketch, "E182", {"start": v(-13.65, 1.3) * mm, "end": v(-12, 1.3) * mm});
            skLineSegment(sketch, "E183", {"start": v(-13.65, -0.5) * mm, "end": v(-12, -0.5) * mm});
            skLineSegment(sketch, "E184", {"start": v(-13.65, 1.3) * mm, "end": v(-11.11, 3.98) * mm});
            skLineSegment(sketch, "E185", {"start": v(-3.5, 1.3) * mm, "end": v(-6.03, 3.98) * mm});
            skLineSegment(sketch, "E186", {"start": v(-12, 1.3) * mm, "end": v(-10.3, 3.09) * mm});
            skLineSegment(sketch, "E187", {"start": v(-5.14, 1.3) * mm, "end": v(-6.84, 3.09) * mm});
            skLineSegment(sketch, "E188.trimOffspring", {"start": v(-10.3, 3.09) * mm, "end": v(-6.84, 3.09) * mm});
            skLineSegment(sketch, "E189", {"start": v(-10.48, 1.3) * mm, "end": v(-10.48, -0.5) * mm});
            skLineSegment(sketch, "E190", {"start": v(-6.67, 1.3) * mm, "end": v(-6.67, -0.5) * mm});
            skLineSegment(sketch, "E191", {"start": v(-10.48, 1.3) * mm, "end": v(-6.67, 1.3) * mm});
            skLineSegment(sketch, "E192.trimOffspring", {"start": v(-5.14, 1.3) * mm, "end": v(-3.5, 1.3) * mm});
            skLineSegment(sketch, "E193", {"start": v(-10.48, -0.5) * mm, "end": v(-6.67, -0.5) * mm});
            skLineSegment(sketch, "E194", {"start": v(-11.11, -3.18) * mm, "end": v(-13.65, -0.5) * mm});
            skLineSegment(sketch, "E195", {"start": v(-6.03, -3.18) * mm, "end": v(-3.5, -0.5) * mm});
            skLineSegment(sketch, "E196", {"start": v(-12, -0.5) * mm, "end": v(-10.3, -2.28) * mm});
            skLineSegment(sketch, "E197", {"start": v(-5.14, -0.5) * mm, "end": v(-6.84, -2.28) * mm});
            skLineSegment(sketch, "E198", {"start": v(-10.3, -2.28) * mm, "end": v(-6.84, -2.28) * mm});
            skLineSegment(sketch, "E199.trimOffspring", {"start": v(-5.14, -0.5) * mm, "end": v(-3.5, -0.5) * mm});
            skLineSegment(sketch, "E200.trimOffspring", {"start": v(-11.11, 3.98) * mm, "end": v(-6.03, 3.98) * mm});
            skLineSegment(sketch, "E201.trimOffspring", {"start": v(0.26, -3.19) * mm, "end": v(2.4, -3.18) * mm});
            skLineSegment(sketch, "E202.trimOffspring", {"start": v(-11.11, -3.18) * mm, "end": v(-6.03, -3.18) * mm});
            skLineSegment(sketch, "E203.trimOffspring", {"start": v(-0.83, 3.98) * mm, "end": v(6.67, 3.98) * mm});
            skPoint(sketch, "E204.start.orphan", {"position": v(-32.17, -11.9) * mm});
            skLineSegment(sketch, "E205", {"start": v(6.67, 3.98) * mm, "end": v(2.4, -3.18) * mm});
            skLineSegment(sketch, "E206", {"start": v(0.26, -3.19) * mm, "end": v(3.45, 2.18) * mm});
            skLineSegment(sketch, "E207", {"start": v(-1.9, 2.18) * mm, "end": v(3.45, 2.18) * mm});
            skLineSegment(sketch, "E208", {"start": v(-1.9, 2.18) * mm, "end": v(-0.83, 3.98) * mm});
            skLineSegment(sketch, "E209", {"start": v(13.65, -3.18) * mm, "end": v(13.65, 3.98) * mm});
            skLineSegment(sketch, "E210", {"start": v(10.25, 3.98) * mm, "end": v(13.65, 3.98) * mm});
            skLineSegment(sketch, "E211", {"start": v(10.95, -3.18) * mm, "end": v(13.65, -3.18) * mm});
            skLineSegment(sketch, "E212", {"start": v(10.95, -3.18) * mm, "end": v(10.95, 1.85) * mm});
            skLineSegment(sketch, "E213", {"start": v(10.25, 3.98) * mm, "end": v(8.25, 2.15) * mm});
            skLineSegment(sketch, "E214", {"start": v(10.95, 1.85) * mm, "end": v(9.64, 0.64) * mm});
            skLineSegment(sketch, "E215", {"start": v(8.25, 2.15) * mm, "end": v(9.64, 0.64) * mm});
            const initialGuessF8  = {"E181": [-0.01524, -0.00841, 1, 0, 0.0036]};
            skSetInitialGuess(sketch, initialGuessF8);
            skSolve(sketch);
        }
        {
            var Q0;
            Q0=makeQuery(id+"F8.imprint","IMPRINT",FACE,{"disambiguationData":[TD([[makeQuery(id+"F8.imprint","IMPRINT",EDGE,{"derivedFrom":sQuery(id+"F8.wireOp",EDGE,"E181.sketch_text.stroke-0")}),-1.0]])]});
            var Q1;
            Q1=makeQuery(id+"F8.imprint","IMPRINT",FACE,{"disambiguationData":[TD([[makeQuery(id+"F8.imprint","IMPRINT",EDGE,{"derivedFrom":sQuery(id+"F8.wireOp",EDGE,"E181.sketch_text.stroke-13")}),-1.0]])]});
            var Q2;
            Q2=makeQuery(id+"F8.imprint","IMPRINT",FACE,{"disambiguationData":[TD([[makeQuery(id+"F8.imprint","IMPRINT",EDGE,{"derivedFrom":sQuery(id+"F8.wireOp",EDGE,"E181.sketch_text.stroke-34")}),-1.0]])]});
            var Q3;
            Q3=makeQuery(id+"F8.imprint","IMPRINT",FACE,{"disambiguationData":[TD([[makeQuery(id+"F8.imprint","IMPRINT",EDGE,{"derivedFrom":sQuery(id+"F8.wireOp",EDGE,"E181.sketch_text.stroke-55")}),-1.0]])]});
            var Q4;
            Q4=makeQuery(id+"F8.imprint","IMPRINT",FACE,{"disambiguationData":[TD([[makeQuery(id+"F8.imprint","IMPRINT",EDGE,{"derivedFrom":sQuery(id+"F8.wireOp",EDGE,"E181.sketch_text.stroke-68")}),-1.0]])]});
            extrude(context, id + "F9", {"entities" : qUnion([Q0, Q1, Q2, Q3, Q4]), "operationType" : NewBodyOperationType.REMOVE, "oppositeDirection" : true, "depth" : 0.2 * mm});
        }
        {
            var Q0;
            Q0=makeQuery(id+"F8.imprint","IMPRINT",FACE,{"disambiguationData":[TD([[makeQuery(id+"F8.imprint","IMPRINT",EDGE,{"derivedFrom":sQuery(id+"F8.wireOp",EDGE,"E181.sketch_text.stroke-117")}),-1.0]])]});
            var Q1;
            Q1=makeQuery(id+"F8.imprint","IMPRINT",FACE,{"disambiguationData":[TD([[makeQuery(id+"F8.imprint","IMPRINT",EDGE,{"derivedFrom":sQuery(id+"F8.wireOp",EDGE,"E181.sketch_text.stroke-96")}),-1.0]])]});
            var Q2;
            Q2=makeQuery(id+"F8.imprint","IMPRINT",FACE,{"disambiguationData":[TD([[makeQuery(id+"F8.imprint","IMPRINT",EDGE,{"derivedFrom":sQuery(id+"F8.wireOp",EDGE,"E181.sketch_text.stroke-83")}),-1.0]])]});
            var Q3;
            Q3=makeQuery(id+"F8.imprint","IMPRINT",FACE,{"disambiguationData":[TD([[makeQuery(id+"F8.imprint","IMPRINT",EDGE,{"derivedFrom":sQuery(id+"F8.wireOp",EDGE,"E181.sketch_text.stroke-112")}),-1.0]])]});
            var Q4;
            Q4=makeQuery(id+"F8.imprint","IMPRINT",FACE,{"disambiguationData":[TD([[makeQuery(id+"F8.imprint","IMPRINT",EDGE,{"derivedFrom":sQuery(id+"F8.wireOp",EDGE,"E181.sketch_text.stroke-127")}),-1.0]])]});
            var Q5;
            Q5=makeQuery(id+"F8.imprint","IMPRINT",FACE,{"disambiguationData":[TD([[makeQuery(id+"F8.imprint","IMPRINT",EDGE,{"derivedFrom":sQuery(id+"F8.wireOp",EDGE,"E181.sketch_text.stroke-139")}),-1.0]])]});
            extrude(context, id + "F10", {"entities" : qUnion([Q0, Q1, Q2, Q3, Q4, Q5]), "operationType" : NewBodyOperationType.REMOVE, "oppositeDirection" : true, "depth" : 0.2 * mm});
        }
        {
            var Q0;
            Q0=makeQuery(id+"F8.imprint","IMPRINT",FACE,{"disambiguationData":[TD([[makeQuery(id+"F8.imprint","IMPRINT",EDGE,{"derivedFrom":sQuery(id+"F8.wireOp",EDGE,"E182")}),1.0]])]});
            var Q1;
            Q1=makeQuery(id+"F8.imprint","IMPRINT",FACE,{"disambiguationData":[TD([[makeQuery(id+"F8.imprint","IMPRINT",EDGE,{"derivedFrom":sQuery(id+"F8.wireOp",EDGE,"E189")}),1.0]])]});
            var Q2;
            Q2=makeQuery(id+"F8.imprint","IMPRINT",FACE,{"disambiguationData":[TD([[makeQuery(id+"F8.imprint","IMPRINT",EDGE,{"derivedFrom":sQuery(id+"F8.wireOp",EDGE,"E183")}),-1.0]])]});
            var Q3;
            Q3=makeQuery(id+"F8.imprint","IMPRINT",FACE,{"disambiguationData":[TD([[makeQuery(id+"F8.imprint","IMPRINT",EDGE,{"derivedFrom":sQuery(id+"F8.wireOp",EDGE,"E201.trimOffspring")}),1.0]])]});
            var Q4;
            Q4=makeQuery(id+"F8.imprint","IMPRINT",FACE,{"disambiguationData":[TD([[makeQuery(id+"F8.imprint","IMPRINT",EDGE,{"derivedFrom":sQuery(id+"F8.wireOp",EDGE,"E209")}),1.0]])]});
            extrude(context, id + "F11", {"entities" : qUnion([Q0, Q1, Q2, Q3, Q4]), "operationType" : NewBodyOperationType.REMOVE, "oppositeDirection" : true, "depth" : 0.2 * mm});
        }
    });
